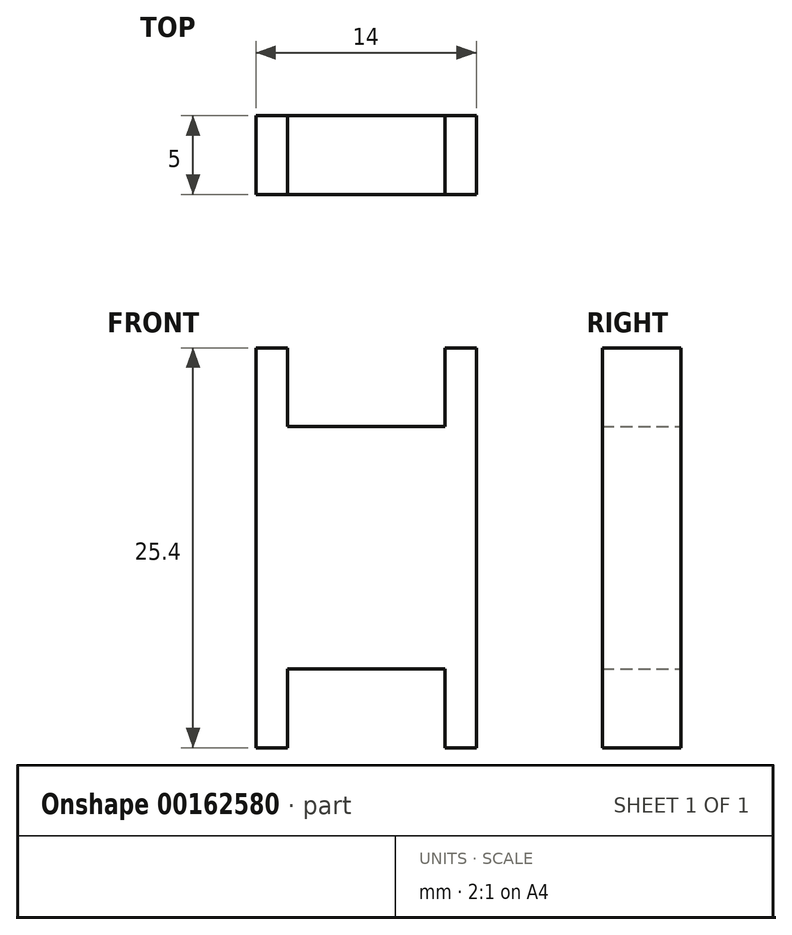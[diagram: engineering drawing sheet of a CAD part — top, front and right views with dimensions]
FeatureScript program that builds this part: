
annotation { "Feature Type Name" : "Feature", "Feature Type Description" : "" }
export const myFeature = defineFeature(function(context is Context, id is Id, definition is map)
    precondition{}
    {
        {
            var Q0;
            Q0=qCreatedBy(makeId("Front.planeOp"),FACE);
            var sketch = newSketch(context, id + "F0", { "sketchPlane" : qUnion([Q0])});
            skLineSegment(sketch, "E0.bottom", {"start": v(7, 7.7) * mm, "end": v(-7, 7.7) * mm});
            skLineSegment(sketch, "E0.top", {"start": v(7, -7.7) * mm, "end": v(-7, -7.7) * mm});
            skLineSegment(sketch, "E0.left", {"start": v(7, 7.7) * mm, "end": v(7, -7.7) * mm});
            skLineSegment(sketch, "E0.right", {"start": v(-7, 7.7) * mm, "end": v(-7, -7.7) * mm});
            skPoint(sketch, "E0.middle", {"position": v(0, 0) * mm});
            skLineSegment(sketch, "E1.bottom", {"start": v(-7, -7.7) * mm, "end": v(-5, -7.7) * mm});
            skLineSegment(sketch, "E1.top", {"start": v(-7, -12.7) * mm, "end": v(-5, -12.7) * mm});
            skLineSegment(sketch, "E1.left", {"start": v(-7, -7.7) * mm, "end": v(-7, -12.7) * mm});
            skLineSegment(sketch, "E1.right", {"start": v(-5, -7.7) * mm, "end": v(-5, -12.7) * mm});
            skLineSegment(sketch, "E2.bottom", {"start": v(-7, 7.7) * mm, "end": v(-5, 7.7) * mm});
            skLineSegment(sketch, "E2.top", {"start": v(-7, 12.7) * mm, "end": v(-5, 12.7) * mm});
            skLineSegment(sketch, "E2.left", {"start": v(-7, 7.7) * mm, "end": v(-7, 12.7) * mm});
            skLineSegment(sketch, "E2.right", {"start": v(-5, 7.7) * mm, "end": v(-5, 12.7) * mm});
            skLineSegment(sketch, "E3.bottom", {"start": v(7, 7.7) * mm, "end": v(5, 7.7) * mm});
            skLineSegment(sketch, "E3.top", {"start": v(7, 12.7) * mm, "end": v(5, 12.7) * mm});
            skLineSegment(sketch, "E3.left", {"start": v(7, 7.7) * mm, "end": v(7, 12.7) * mm});
            skLineSegment(sketch, "E3.right", {"start": v(5, 7.7) * mm, "end": v(5, 12.7) * mm});
            skLineSegment(sketch, "E4.bottom", {"start": v(7, -7.7) * mm, "end": v(5, -7.7) * mm});
            skLineSegment(sketch, "E4.top", {"start": v(7, -12.7) * mm, "end": v(5, -12.7) * mm});
            skLineSegment(sketch, "E4.left", {"start": v(7, -7.7) * mm, "end": v(7, -12.7) * mm});
            skLineSegment(sketch, "E4.right", {"start": v(5, -7.7) * mm, "end": v(5, -12.7) * mm});
            skSolve(sketch);
        }
        {
            var Q0;
            Q0 = qSketchRegion(id + "F0", true);
            extrude(context, id + "F1", {"entities" : qUnion([Q0]), "depth" : 5 * mm});
        }
    });
